# Revit family: Dauphin-Bosse S2_Dialogue Pod
name_source: partatom
category: Casework
units: mm (PartAtom-declared; Revit-internal decimal feet)

## family parameters
Always vertical = Yes
Cut with Voids When Loaded = No
Room Calculation Point = No
Shared = No
Work Plane-Based = No

## types (3) — shared parameters
Depth = 1348 mm  [stored 4.42257 ft]
Door Handle Material = Bosse_Door Handle Material
Electrical Connection = Bosse_Door Metal Material
External Cladding Material = Bosse_Panel Exterior Material
Floor Material = Bosse_Fabric Divina Asphalt Grey
Glass Material = Bosse_Panel Glass Material
Height = 2400 mm
Internal Cladding Material = Bosse_Fabric Divina Asphalt Grey
Manufacturer = Dauphin North America
Metal Strip Material = Bosse_Door Metal Material
Model = BP2D_P92X54X94
Panel_Side_Depth = 1169 mm
Profile Materials = Bosse_Panel Exterior Material
Seat Cover Material = Bosse_Seat Cover
Seat Material = Bosse_Fabric Divina Asphalt Grey
Table Leg = Bosse_Table Leg Material
Table Top = Bosse_Table Top Material
Type Comments = Bosse Dialogue Pod S2
URL = www.dauphin.co.za
Width = 2327 mm  [stored 7.63451 ft]

## per-type parameters (varying)
| type | Benches & Table | Description | Electrical Fixture |
| BP2D_P92X54X94 - Seats & Table with Electrical Fixuture | Yes | Seats & Table with Electrical Fixuture | Yes |
| BP2D_P92X54X94 - Seats & Table | Yes | Dialogue Pod with Seats & Table | No |
| BP2D_P92X54X94 - Dialogue Pod Only | No | Dialogue Pod Only | No |

note: [stored X ft] marks values corroborated as IEEE doubles in the binary element streams (Revit-internal decimal feet)

## geometry (parser evidence)
native form markers: Sweep x21
no freeform markers — native parametric forms only
